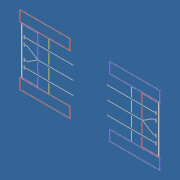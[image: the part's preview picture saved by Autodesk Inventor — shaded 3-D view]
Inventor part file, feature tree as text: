
AUTODESK INVENTOR PART (.ipt)
format: ipt  version: unknown  size: 440,320 bytes
history: native  units: in
note: dims shown in document units (in); Inventor stores cm internally (conversion verified against a paired STEP export)
features: extrude x7, sketch x1
ambient origin geometry x8: Origin, YZ Plane, XZ Plane, XY Plane, X Axis, Y Axis, Z Axis, Center Point
bodies: Solid1 (feature_tree)
feature tree (8):
  sketch  "Sketch1"  dims[d0=320.971in d1=648.719in d2=324.3595in d3=160.4855in d5=3.0in d6=90.0in d7=3.0in d8=0.25in d9=0.0in d10=0.25in d11=0.0in d12=3.0in d13=3.0in d14=2.0in d15=12.0in d16=23.5in d17=4.0in d18=14.0in d19=99.11in d20=99.11in d21=12.0in d22=30.0in d23=30.0in d24=1.0in d26=6.0in d27=6.0in d28=6.0in d29=6.0in d30=6.0in d31=6.0in d33=3.0in d34=87.0in d35=2.0in d37=6.0in d38=6.0in d39=6.0in d40=6.0in d41=6.0in d42=6.0in d44=48.0in d45=2.0in d46=1.0in d47=26.2485in d48=51.783in d49=51.0in d50=51.783in d51=7.5in d52=0.25in d53=0.0in d54=0.25in d55=0.0in d56=0.25in d57=0.0in d58=0.05in d59=0.05in d60=0.25in d61=0.0in d62=0.25in d63=0.0in]
  extrude  "Extrusion1"  Depth=648.719in
  extrude  "Extrusion2"  Depth=324.3595in
  extrude  "Extrusion3"  Depth=160.4855in
  extrude  "Extrusion4"  Depth=3.0in
  extrude  "Extrusion5"  Depth=90.0in
  extrude  "Extrusion6"  Depth=3.0in
  extrude  "Extrusion7"  Depth=0.25in TaperAngle=0.0deg
